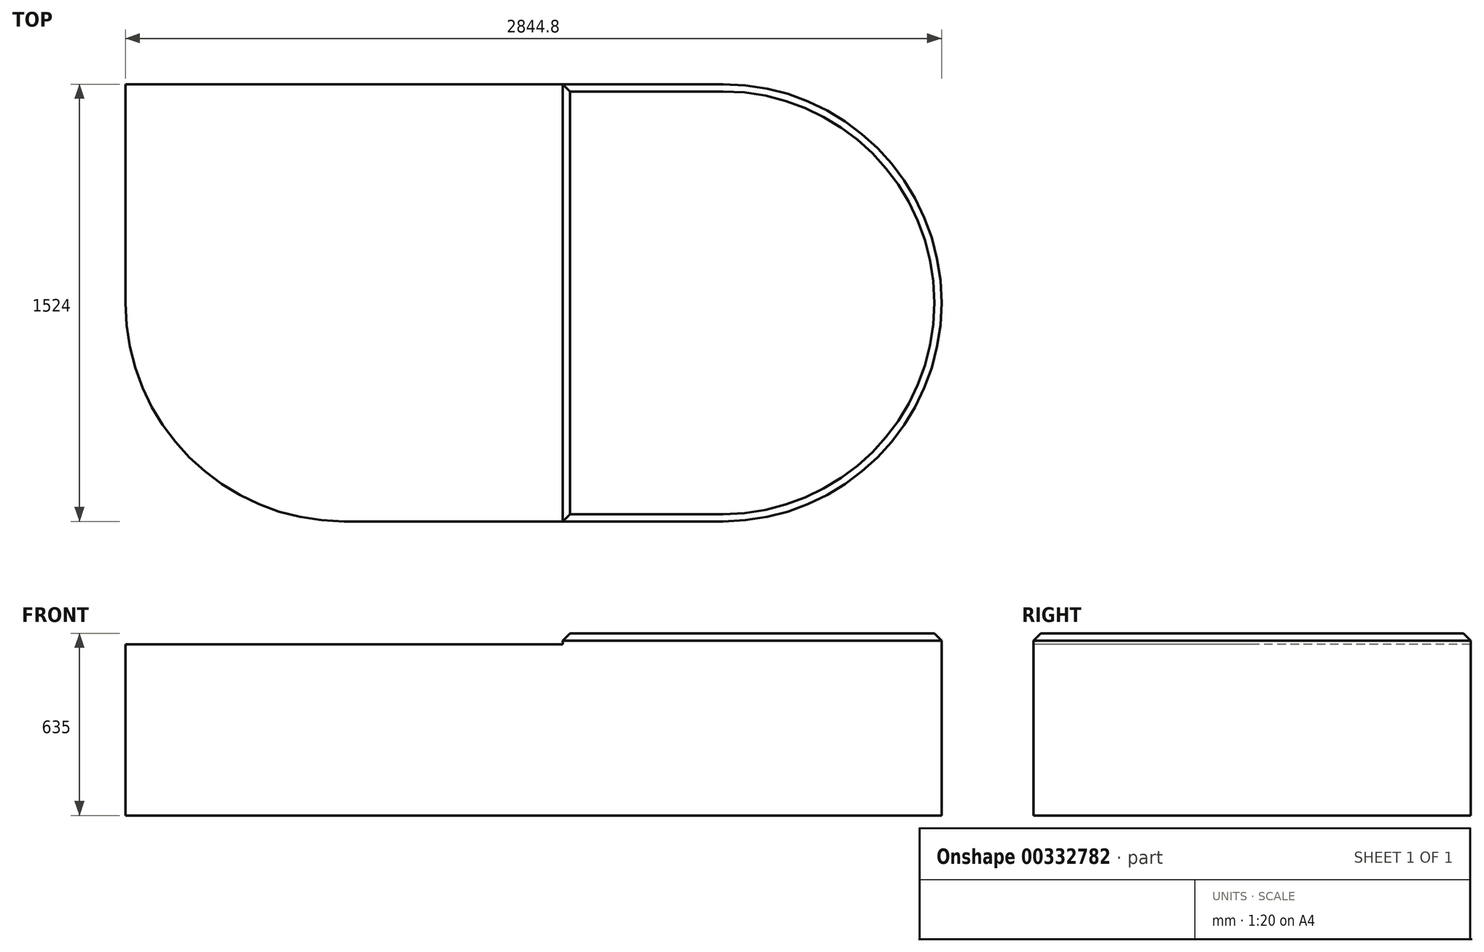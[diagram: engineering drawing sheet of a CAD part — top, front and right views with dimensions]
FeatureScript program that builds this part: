
annotation { "Feature Type Name" : "Feature", "Feature Type Description" : "" }
export const myFeature = defineFeature(function(context is Context, id is Id, definition is map)
    precondition{}
    {
        {
            var Q0;
            Q0=qCreatedBy(makeId("Top.planeOp"),FACE);
            var sketch = newSketch(context, id + "F0", { "sketchPlane" : qUnion([Q0])});
            skLineSegment(sketch, "E0.bottom", {"start": v(-1011.27, 750.4) * mm, "end": v(1833.53, 750.4) * mm});
            skLineSegment(sketch, "E0.top", {"start": v(-1011.27, -773.6) * mm, "end": v(1833.53, -773.6) * mm});
            skLineSegment(sketch, "E0.left", {"start": v(-1011.27, 750.4) * mm, "end": v(-1011.27, -773.6) * mm});
            skLineSegment(sketch, "E0.right", {"start": v(1833.53, 750.4) * mm, "end": v(1833.53, -773.6) * mm});
            skSolve(sketch);
        }
        {
            var Q0;
            Q0=makeQuery(id+"F0.imprint","IMPRINT",FACE,{"disambiguationData":[TD([[makeQuery(id+"F0.imprint","IMPRINT",EDGE,{"derivedFrom":sQuery(id+"F0.wireOp",EDGE,"E0.bottom")}),-1.0]])]});
            extrude(context, id + "F1", {"entities" : qUnion([Q0]), "depth" : 635 * mm});
        }
        {
            var Q0;
            Q0=makeQuery(id+"F1.opExtrude","CAP_FACE",FACE,{"disambiguationData":[OSD([sQuery(id+"F0.wireOp",EDGE,"E0.bottom"),sQuery(id+"F0.wireOp",EDGE,"E0.top"),sQuery(id+"F0.wireOp",EDGE,"E0.left"),sQuery(id+"F0.wireOp",EDGE,"E0.right")])],"isStart":false});
            var sketch = newSketch(context, id + "F2", { "sketchPlane" : qUnion([Q0])});
            skLineSegment(sketch, "E1.bottom", {"start": v(-1011.27, 750.4) * mm, "end": v(512.73, 750.4) * mm});
            skLineSegment(sketch, "E1.top", {"start": v(-1011.27, -773.6) * mm, "end": v(512.73, -773.6) * mm});
            skLineSegment(sketch, "E1.left", {"start": v(-1011.27, 750.4) * mm, "end": v(-1011.27, -773.6) * mm});
            skLineSegment(sketch, "E1.right", {"start": v(512.73, 750.4) * mm, "end": v(512.73, -773.6) * mm});
            skSolve(sketch);
        }
        {
            var Q0;
            Q0=makeQuery(id+"F2.imprint","IMPRINT",FACE,{"disambiguationData":[TD([[makeQuery(id+"F2.imprint","IMPRINT",EDGE,{"derivedFrom":sQuery(id+"F2.wireOp",EDGE,"E1.bottom")}),-1.0]])]});
            extrude(context, id + "F3", {"entities" : qUnion([Q0]), "operationType" : NewBodyOperationType.REMOVE, "endBound" : BoundingType.SYMMETRIC, "oppositeDirection" : true, "depth" : 127 * mm});
        }
        {
            var Q0;
            Q0=makeQuery(id+"F1.opExtrude","SWEPT_EDGE",EDGE,{"disambiguationData":[OSD([sQuery(id+"F0.wireOp",EDGE,"E0.top"),sQuery(id+"F0.wireOp",EDGE,"E0.left")])]});
            fillet(context, id + "F4", {"entities" : qUnion([Q0]), "radius" : 762 * mm, "tangentPropagation" : true, "allowEdgeOverflow" : false});
        }
        {
            var Q0;
            Q0=makeQuery(id+"F3.boolean.opBoolean","INTERSECT",EDGE,{"derivedFrom":[makeQuery(id+"F1.opExtrude","CAP_FACE",FACE,{"disambiguationData":[OSD([sQuery(id+"F0.wireOp",EDGE,"E0.bottom"),sQuery(id+"F0.wireOp",EDGE,"E0.top"),sQuery(id+"F0.wireOp",EDGE,"E0.left"),sQuery(id+"F0.wireOp",EDGE,"E0.right")])],"isStart":false}),makeQuery(id+"F3.opExtrude","SWEPT_FACE",FACE,{"disambiguationData":[OSD([sQuery(id+"F2.wireOp",EDGE,"E1.right")])]})]});
            var Q1;
            Q1=makeQuery(id+"F1.opExtrude","CAP_EDGE",EDGE,{"disambiguationData":[OSD([sQuery(id+"F0.wireOp",EDGE,"E0.top")])],"isStart":false});
            var Q2;
            Q2=makeQuery(id+"F1.opExtrude","CAP_EDGE",EDGE,{"disambiguationData":[OSD([sQuery(id+"F0.wireOp",EDGE,"E0.right")])],"isStart":false});
            var Q3;
            Q3=makeQuery(id+"F1.opExtrude","CAP_EDGE",EDGE,{"disambiguationData":[OSD([sQuery(id+"F0.wireOp",EDGE,"E0.bottom")])],"isStart":false});
            chamfer(context, id + "F5", {"entities" : qUnion([Q0, Q1, Q2, Q3]), "width" : 25.4 * mm, "tangentPropagation" : true});
        }
        {
            var Q0;
            Q0=makeQuery(id+"F1.opExtrude","SWEPT_EDGE",EDGE,{"disambiguationData":[OSD([sQuery(id+"F0.wireOp",EDGE,"E0.top"),sQuery(id+"F0.wireOp",EDGE,"E0.right")])]});
            var Q1;
            Q1=makeQuery(id+"F1.opExtrude","SWEPT_EDGE",EDGE,{"disambiguationData":[OSD([sQuery(id+"F0.wireOp",EDGE,"E0.bottom"),sQuery(id+"F0.wireOp",EDGE,"E0.right")])]});
            fillet(context, id + "F6", {"entities" : qUnion([Q0, Q1]), "radius" : 762 * mm, "tangentPropagation" : true, "allowEdgeOverflow" : false});
        }
        {
            var Q0;
            {var subQ0=sQuery(id+"F0.wireOp",EDGE,"E0.right");var subQ1=sQuery(id+"F0.wireOp",EDGE,"E0.top");Q0=makeQuery(id+"F6.opFillet","BLEND_EDGE",EDGE,{"blendedFrom":[makeQuery(id+"F1.opExtrude","SWEPT_EDGE",EDGE,{"disambiguationData":[OSD([subQ1,subQ0])]}),makeQuery(id+"F1.opExtrude","CAP_FACE",FACE,{"disambiguationData":[OSD([sQuery(id+"F0.wireOp",EDGE,"E0.bottom"),subQ1,sQuery(id+"F0.wireOp",EDGE,"E0.left"),subQ0])],"isStart":false})],"blendedInto":[makeQuery(id+"F1.opExtrude","CAP_FACE",FACE,{"disambiguationData":[OSD([sQuery(id+"F0.wireOp",EDGE,"E0.bottom"),subQ1,sQuery(id+"F0.wireOp",EDGE,"E0.left"),subQ0])],"isStart":false})]});}
            var Q1;
            {var subQ0=sQuery(id+"F0.wireOp",EDGE,"E0.right");var subQ1=sQuery(id+"F0.wireOp",EDGE,"E0.bottom");Q1=makeQuery(id+"F6.opFillet","BLEND_EDGE",EDGE,{"blendedFrom":[makeQuery(id+"F1.opExtrude","SWEPT_EDGE",EDGE,{"disambiguationData":[OSD([subQ1,subQ0])]}),makeQuery(id+"F1.opExtrude","CAP_FACE",FACE,{"disambiguationData":[OSD([subQ1,sQuery(id+"F0.wireOp",EDGE,"E0.top"),sQuery(id+"F0.wireOp",EDGE,"E0.left"),subQ0])],"isStart":false})],"blendedInto":[makeQuery(id+"F1.opExtrude","CAP_FACE",FACE,{"disambiguationData":[OSD([subQ1,sQuery(id+"F0.wireOp",EDGE,"E0.top"),sQuery(id+"F0.wireOp",EDGE,"E0.left"),subQ0])],"isStart":false})]});}
            chamfer(context, id + "F7", {"entities" : qUnion([Q0, Q1]), "width" : 25.4 * mm, "tangentPropagation" : true});
        }
        {
            var Q0;
            Q0=makeQuery(id+"F3.boolean.opBoolean","COPY",FACE,{"derivedFrom":makeQuery(id+"F3.opExtrude","CAP_FACE",FACE,{"disambiguationData":[OSD([sQuery(id+"F2.wireOp",EDGE,"E1.bottom"),sQuery(id+"F2.wireOp",EDGE,"E1.top"),sQuery(id+"F2.wireOp",EDGE,"E1.left"),sQuery(id+"F2.wireOp",EDGE,"E1.right")])],"isStart":false})});
            extrude(context, id + "F8", {"entities" : qUnion([Q0]), "operationType" : NewBodyOperationType.ADD, "depth" : 25.4 * mm});
        }
    });
